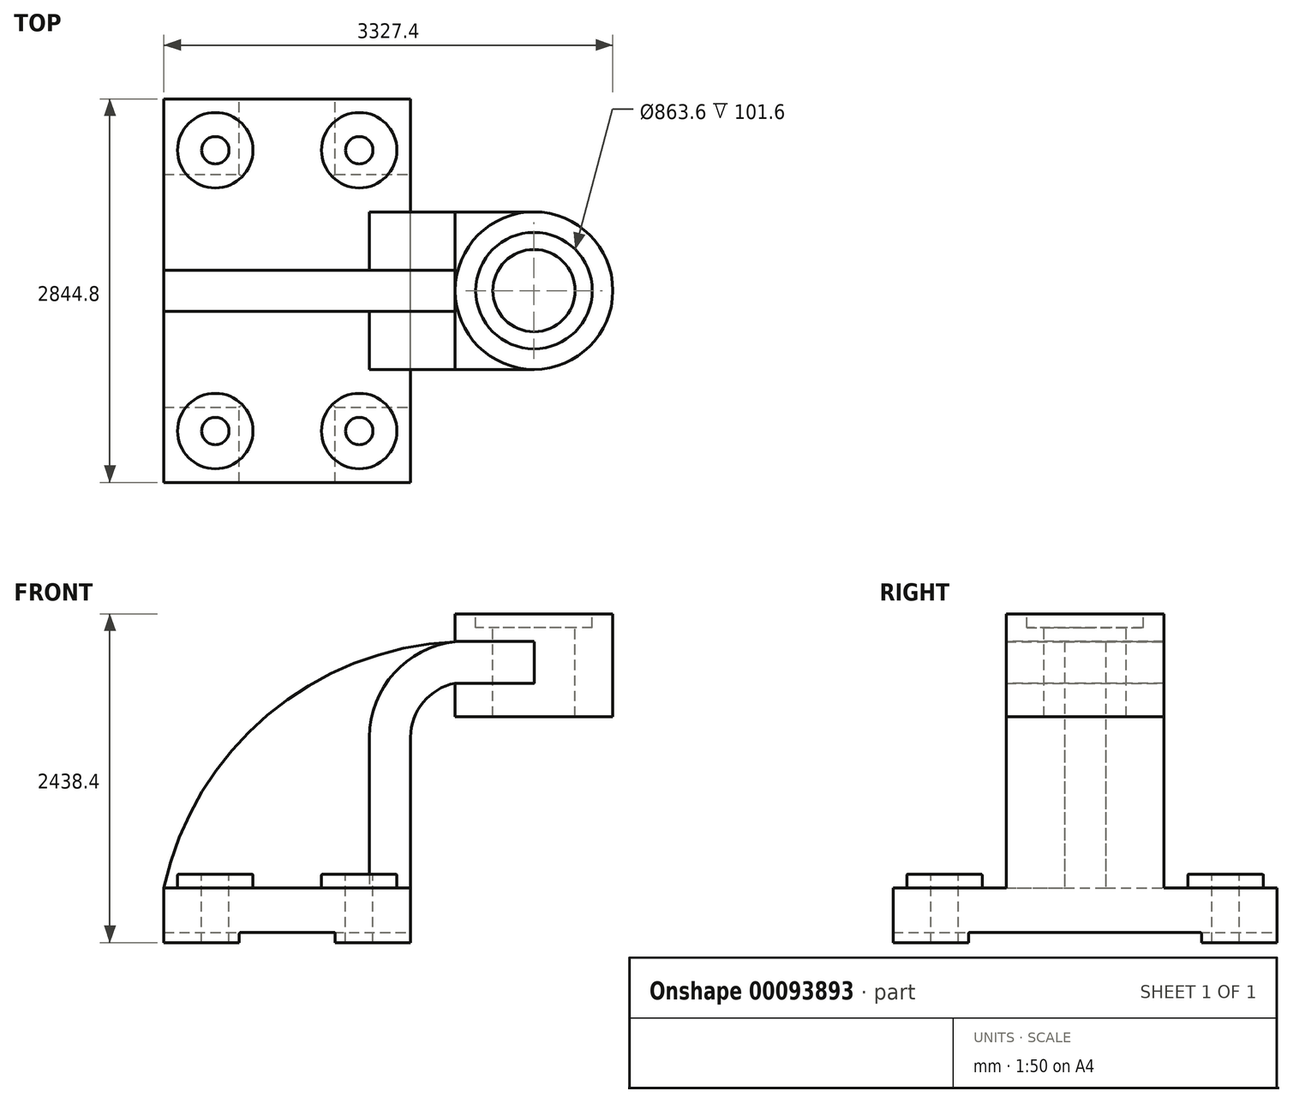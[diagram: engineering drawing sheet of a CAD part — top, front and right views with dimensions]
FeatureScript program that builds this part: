
annotation { "Feature Type Name" : "Feature", "Feature Type Description" : "" }
export const myFeature = defineFeature(function(context is Context, id is Id, definition is map)
    precondition{}
    {
        {
            var Q0;
            Q0=qCreatedBy(makeId("Front.planeOp"),FACE);
            var sketch = newSketch(context, id + "F0", { "sketchPlane" : qUnion([Q0])});
            skLineSegment(sketch, "E0", {"start": v(0, 0) * mm, "end": v(0, 1117.6) * mm});
            skLineSegment(sketch, "E1", {"start": v(406.4, 1524) * mm, "end": v(914.4, 1524) * mm});
            skLineSegment(sketch, "E2", {"start": v(-563.11, 0) * mm, "end": v(-1828.8, 0) * mm});
            skLineSegment(sketch, "E3", {"start": v(-1828.8, 0) * mm, "end": v(-1828.8, -406.4) * mm});
            skLineSegment(sketch, "E4", {"start": v(-1828.8, -406.4) * mm, "end": v(0, -406.4) * mm});
            skLineSegment(sketch, "E5", {"start": v(0, -406.4) * mm, "end": v(0, 0) * mm});
            skLineSegment(sketch, "E6", {"start": v(914.4, 1828.8) * mm, "end": v(914.4, 1524) * mm});
            skLineSegment(sketch, "E7", {"start": v(330.2, 2032) * mm, "end": v(330.2, 1270) * mm});
            skLineSegment(sketch, "E8", {"start": v(330.2, 1270) * mm, "end": v(1498.6, 1270) * mm});
            skLineSegment(sketch, "E9", {"start": v(1498.6, 1270) * mm, "end": v(1498.6, 2032) * mm});
            skLineSegment(sketch, "E10", {"start": v(1498.6, 2032) * mm, "end": v(330.2, 2032) * mm});
            skArc(sketch, "E11", {"start": v(330.2, 1824.7) * mm, "mid": v(-1060.76, 1280.87) * mm, "end": v(-1828.8, 0) * mm});
            skLineSegment(sketch, "E12", {"start": v(0, 0) * mm, "end": v(-1828.8, 0) * mm});
            skPoint(sketch, "E13.visualSharp", {"position": v(0, 1524) * mm});
            skArc(sketch, "E13.filletArc", {"start": v(406.4, 1524) * mm, "mid": v(119.03, 1404.97) * mm, "end": v(0, 1117.6) * mm});
            skLineSegment(sketch, "E14", {"start": v(-304.8, 1117.6) * mm, "end": v(-304.8, 0) * mm});
            skArc(sketch, "E15", {"start": v(-304.8, 1117.6) * mm, "mid": v(-122.75, 1592.8) * mm, "end": v(330.2, 1824.7) * mm});
            skPoint(sketch, "E16.endSnap0", {"position": v(-1828.8, -203.2) * mm});
            skLineSegment(sketch, "E17", {"start": v(-558.8, -406.4) * mm, "end": v(-558.8, -342.9) * mm});
            skLineSegment(sketch, "E18", {"start": v(-571.5, -330.2) * mm, "end": v(-1257.3, -330.2) * mm});
            skLineSegment(sketch, "E19", {"start": v(-1270, -342.9) * mm, "end": v(-1270, -406.4) * mm});
            skLineSegment(sketch, "E20", {"start": v(914.4, 2032) * mm, "end": v(914.4, 1270) * mm});
            skPoint(sketch, "E21", {"position": v(330.2, 1824.7) * mm});
            skPoint(sketch, "E22", {"position": v(330.2, 1516.8) * mm});
            skPoint(sketch, "E23.visualSharp", {"position": v(-558.8, -330.2) * mm});
            skArc(sketch, "E23.filletArc", {"start": v(-558.8, -342.9) * mm, "mid": v(-562.52, -333.92) * mm, "end": v(-571.5, -330.2) * mm});
            skPoint(sketch, "E24.visualSharp", {"position": v(-1270, -330.2) * mm});
            skArc(sketch, "E24.filletArc", {"start": v(-1257.3, -330.2) * mm, "mid": v(-1266.28, -333.92) * mm, "end": v(-1270, -342.9) * mm});
            skSolve(sketch);
        }
        {
            var Q0;
            Q0=qCreatedBy(makeId("Top.planeOp"),FACE);
            var sketch = newSketch(context, id + "F1", { "sketchPlane" : qUnion([Q0])});
            skLineSegment(sketch, "E25", {"start": v(-1828.8, 0) * mm, "end": v(-1828.8, 1422.4) * mm});
            skLineSegment(sketch, "E26", {"start": v(-1828.8, 1422.4) * mm, "end": v(0, 1422.4) * mm});
            skLineSegment(sketch, "E27", {"start": v(0, 1422.4) * mm, "end": v(0, -1422.4) * mm});
            skLineSegment(sketch, "E28", {"start": v(0, -1422.4) * mm, "end": v(-1828.8, -1422.4) * mm});
            skLineSegment(sketch, "E29", {"start": v(-1828.8, -1422.4) * mm, "end": v(-1828.8, 0) * mm});
            skCircle(sketch, "E30", {"center": v(-1447.8, -1041.4) * mm, "radius": 279.4 * mm});
            skCircle(sketch, "E31", {"center": v(-1447.8, 1041.4) * mm, "radius": 279.4 * mm});
            skCircle(sketch, "E32", {"center": v(-381, 1041.4) * mm, "radius": 279.4 * mm});
            skCircle(sketch, "E33", {"center": v(-381, -1041.4) * mm, "radius": 279.4 * mm});
            skCircle(sketch, "E34", {"center": v(-1447.8, 1041.4) * mm, "radius": 101.6 * mm});
            skCircle(sketch, "E35", {"center": v(-381, 1041.4) * mm, "radius": 101.6 * mm});
            skCircle(sketch, "E36", {"center": v(-1447.8, -1041.4) * mm, "radius": 101.6 * mm});
            skCircle(sketch, "E37", {"center": v(-381, -1041.4) * mm, "radius": 101.6 * mm});
            skSolve(sketch);
        }
        {
            var Q0;
            {var subQ1=sQuery(id+"F0.wireOp",EDGE,"E9");Q0=makeQuery(id+"F0.imprint","IMPRINT",FACE,{"disambiguationData":[TD([[makeQuery(id+"F0.imprint","IMPRINT",EDGE,{"derivedFrom":subQ1}),1.0]])]});}
            var Q1;
            Q1=sQuery(id+"F0.wireOp",EDGE,"E20");
            revolve(context, id + "F2", {"entities" : qUnion([Q0]), "axis" : qUnion([Q1]), "revolveType" : RevolveType.FULL});
        }
        {
            var Q0;
            {var subQ8=sQuery(id+"F0.wireOp",EDGE,"E0");Q0=makeQuery(id+"F0.imprint","IMPRINT",FACE,{"disambiguationData":[TD([[makeQuery(id+"F0.imprint","IMPRINT",EDGE,{"derivedFrom":subQ8}),1.0]])]});}
            extrude(context, id + "F3", {"entities" : qUnion([Q0]), "endBound" : BoundingType.SYMMETRIC, "depth" : 1168.4 * mm});
        }
        {
            var Q0;
            Q0=makeQuery(id+"F3.opExtrude","SWEPT_FACE",FACE,{"disambiguationData":[OSD([sQuery(id+"F0.wireOp",EDGE,"E7")])]});
            extrude(context, id + "F4", {"entities" : qUnion([Q0]), "depth" : 584.57 * mm});
        }
        {
            var Q0;
            Q0=makeQuery(id+"F2.opRevolve","SWEPT_BODY",BODY,{"disambiguationData":[OSD([sQuery(id+"F0.wireOp",EDGE,"E8"),sQuery(id+"F0.wireOp",EDGE,"E9"),sQuery(id+"F0.wireOp",EDGE,"E10"),sQuery(id+"F0.wireOp",EDGE,"E20")])]});
            var Q1;
            Q1=makeQuery(id+"F3.opExtrude","SWEPT_BODY",BODY,{"disambiguationData":[OSD([sQuery(id+"F0.wireOp",EDGE,"E0"),sQuery(id+"F0.wireOp",EDGE,"E1"),sQuery(id+"F0.wireOp",EDGE,"Te8mhpom-QYgg-O1N1-Xy0P-BGKtfm83w9Aw"),sQuery(id+"F0.wireOp",EDGE,"E7"),sQuery(id+"F0.wireOp",EDGE,"E11"),sQuery(id+"F0.wireOp",EDGE,"E12"),sQuery(id+"F0.wireOp",EDGE,"E13.filletArc"),sQuery(id+"F0.wireOp",EDGE,"E14"),sQuery(id+"F0.wireOp",EDGE,"E15")])]});
            var Q2;
            Q2=makeQuery(id+"F4.opExtrude","SWEPT_BODY",BODY,{"disambiguationData":[OSD([sQuery(id+"F0.wireOp",EDGE,"E7")])]});
            booleanBodies(context, id + "F5", {"operationType" : BooleanOperationType.UNION, "tools" : qUnion([Q0, Q1, Q2])});
        }
        {
            var Q0;
            {var subQ0=sQuery(id+"F0.wireOp",EDGE,"E14");Q0=makeQuery(id+"F0.imprint","IMPRINT",FACE,{"disambiguationData":[TD([[makeQuery(id+"F0.imprint","IMPRINT",EDGE,{"derivedFrom":subQ0}),-1.0]])]});}
            extrude(context, id + "F6", {"entities" : qUnion([Q0]), "endBound" : BoundingType.SYMMETRIC, "depth" : 304.8 * mm});
        }
        {
            var Q0;
            Q0=makeQuery(id+"F1.imprint","IMPRINT",FACE,{"disambiguationData":[TD([[makeQuery(id+"F1.imprint","IMPRINT",EDGE,{"derivedFrom":sQuery(id+"F1.wireOp",EDGE,"E25")}),-1.0]])]});
            var Q1;
            Q1=makeQuery(id+"F1.imprint","IMPRINT",FACE,{"disambiguationData":[TD([[makeQuery(id+"F1.imprint","IMPRINT",EDGE,{"derivedFrom":sQuery(id+"F1.wireOp",EDGE,"E30")}),1.0]])]});
            var Q2;
            Q2=makeQuery(id+"F1.imprint","IMPRINT",FACE,{"disambiguationData":[TD([[makeQuery(id+"F1.imprint","IMPRINT",EDGE,{"derivedFrom":sQuery(id+"F1.wireOp",EDGE,"E33")}),1.0]])]});
            var Q3;
            Q3=makeQuery(id+"F1.imprint","IMPRINT",FACE,{"disambiguationData":[TD([[makeQuery(id+"F1.imprint","IMPRINT",EDGE,{"derivedFrom":sQuery(id+"F1.wireOp",EDGE,"E32")}),1.0]])]});
            var Q4;
            Q4=makeQuery(id+"F1.imprint","IMPRINT",FACE,{"disambiguationData":[TD([[makeQuery(id+"F1.imprint","IMPRINT",EDGE,{"derivedFrom":sQuery(id+"F1.wireOp",EDGE,"E31")}),1.0]])]});
            extrude(context, id + "F7", {"entities" : qUnion([Q0, Q1, Q2, Q3, Q4]), "operationType" : NewBodyOperationType.ADD, "oppositeDirection" : true, "depth" : 406.4 * mm});
        }
        {
            var Q0;
            Q0=makeQuery(id+"F1.imprint","IMPRINT",FACE,{"disambiguationData":[TD([[makeQuery(id+"F1.imprint","IMPRINT",EDGE,{"derivedFrom":sQuery(id+"F1.wireOp",EDGE,"E30")}),1.0]])]});
            var Q1;
            Q1=makeQuery(id+"F1.imprint","IMPRINT",FACE,{"disambiguationData":[TD([[makeQuery(id+"F1.imprint","IMPRINT",EDGE,{"derivedFrom":sQuery(id+"F1.wireOp",EDGE,"E33")}),1.0]])]});
            var Q2;
            Q2=makeQuery(id+"F1.imprint","IMPRINT",FACE,{"disambiguationData":[TD([[makeQuery(id+"F1.imprint","IMPRINT",EDGE,{"derivedFrom":sQuery(id+"F1.wireOp",EDGE,"E32")}),1.0]])]});
            var Q3;
            Q3=makeQuery(id+"F1.imprint","IMPRINT",FACE,{"disambiguationData":[TD([[makeQuery(id+"F1.imprint","IMPRINT",EDGE,{"derivedFrom":sQuery(id+"F1.wireOp",EDGE,"E31")}),1.0]])]});
            extrude(context, id + "F8", {"entities" : qUnion([Q0, Q1, Q2, Q3]), "operationType" : NewBodyOperationType.ADD, "depth" : 101.6 * mm});
        }
        {
            var Q0;
            {var subQ0=sQuery(id+"F0.wireOp",EDGE,"E17");Q0=makeQuery(id+"F0.imprint","IMPRINT",FACE,{"disambiguationData":[TD([[makeQuery(id+"F0.imprint","IMPRINT",EDGE,{"derivedFrom":subQ0}),1.0]])]});}
            extrude(context, id + "F9", {"entities" : qUnion([Q0]), "operationType" : NewBodyOperationType.REMOVE, "endBound" : BoundingType.THROUGH_ALL, "depth" : 25.4 * mm});
        }
        {
            var Q0;
            {var subQ0=sQuery(id+"F0.wireOp",EDGE,"E17");Q0=makeQuery(id+"F0.imprint","IMPRINT",FACE,{"disambiguationData":[TD([[makeQuery(id+"F0.imprint","IMPRINT",EDGE,{"derivedFrom":subQ0}),1.0]])]});}
            extrude(context, id + "F10", {"entities" : qUnion([Q0]), "operationType" : NewBodyOperationType.REMOVE, "endBound" : BoundingType.THROUGH_ALL, "oppositeDirection" : true, "depth" : 25.4 * mm});
        }
        {
            var Q0;
            {var subQ0=sQuery(id+"F0.wireOp",EDGE,"E15");var subQ1=sQuery(id+"F0.wireOp",EDGE,"E7");var subQ2=makeQuery(id+"F4.opExtrude","SWEPT_FACE",FACE,{"disambiguationData":[OSD([subQ1,subQ0])]});Q0=makeQuery(id+"F5.opBoolean","SPLIT",FACE,{"disambiguationData":[TD([makeQuery(id+"F2.opRevolve","SWEPT_FACE",FACE,{"disambiguationData":[OSD([sQuery(id+"F0.wireOp",EDGE,"E9")])]}),makeQuery(id+"F3.opExtrude","CAP_FACE",FACE,{"disambiguationData":[OSD([sQuery(id+"F0.wireOp",EDGE,"E0"),subQ1,sQuery(id+"F0.wireOp",EDGE,"E12"),sQuery(id+"F0.wireOp",EDGE,"E13.filletArc"),sQuery(id+"F0.wireOp",EDGE,"E14"),subQ0])],"isStart":false}),makeQuery(id+"F3.opExtrude","SWEPT_FACE",FACE,{"disambiguationData":[OSD([subQ0])]}),subQ2,makeQuery(id+"F4.opExtrude","SWEPT_FACE",FACE,{"disambiguationData":[OSD([subQ1]),TDD([makeQuery(id+"F3.opExtrude","CAP_EDGE",EDGE,{"disambiguationData":[OSD([subQ1])],"isStart":false})])]})])],"derivedFrom":subQ2});}
            var Q1;
            {var subQ0=sQuery(id+"F0.wireOp",EDGE,"E15");var subQ1=sQuery(id+"F0.wireOp",EDGE,"E7");var subQ2=makeQuery(id+"F4.opExtrude","SWEPT_FACE",FACE,{"disambiguationData":[OSD([subQ1,subQ0])]});Q1=makeQuery(id+"F5.opBoolean","SPLIT",FACE,{"disambiguationData":[TD([makeQuery(id+"F2.opRevolve","SWEPT_FACE",FACE,{"disambiguationData":[OSD([sQuery(id+"F0.wireOp",EDGE,"E9")])]}),makeQuery(id+"F3.opExtrude","CAP_FACE",FACE,{"disambiguationData":[OSD([sQuery(id+"F0.wireOp",EDGE,"E0"),subQ1,sQuery(id+"F0.wireOp",EDGE,"E12"),sQuery(id+"F0.wireOp",EDGE,"E13.filletArc"),sQuery(id+"F0.wireOp",EDGE,"E14"),subQ0])],"isStart":true}),makeQuery(id+"F3.opExtrude","SWEPT_FACE",FACE,{"disambiguationData":[OSD([subQ0])]}),subQ2,makeQuery(id+"F4.opExtrude","SWEPT_FACE",FACE,{"disambiguationData":[OSD([subQ1]),TDD([makeQuery(id+"F3.opExtrude","CAP_EDGE",EDGE,{"disambiguationData":[OSD([subQ1])],"isStart":true})])]})])],"derivedFrom":subQ2});}
            extrude(context, id + "F11", {"entities" : qUnion([Q0, Q1]), "operationType" : NewBodyOperationType.ADD, "depth" : 2.3 * mm});
        }
        {
            var Q0;
            Q0=makeQuery(id+"F2.opRevolve","SWEPT_FACE",FACE,{"disambiguationData":[OSD([sQuery(id+"F0.wireOp",EDGE,"E10")])]});
            var sketch = newSketch(context, id + "F12", { "sketchPlane" : qUnion([Q0])});
            skPoint(sketch, "E38.0", {"position": v(914.4, 0) * mm});
            skCircle(sketch, "E39", {"center": v(914.4, 0) * mm, "radius": 304.8 * mm});
            skCircle(sketch, "E40", {"center": v(914.4, 0) * mm, "radius": 431.8 * mm});
            skSolve(sketch);
        }
        {
            var Q0;
            Q0=makeQuery(id+"F12.imprint","IMPRINT",FACE,{"disambiguationData":[TD([[makeQuery(id+"F12.imprint","IMPRINT",EDGE,{"derivedFrom":sQuery(id+"F12.wireOp",EDGE,"E39")}),1.0]])]});
            extrude(context, id + "F13", {"entities" : qUnion([Q0]), "operationType" : NewBodyOperationType.REMOVE, "endBound" : BoundingType.THROUGH_ALL, "oppositeDirection" : true, "depth" : 25.4 * mm});
        }
        {
            var Q0;
            Q0=makeQuery(id+"F12.imprint","IMPRINT",FACE,{"disambiguationData":[TD([[makeQuery(id+"F12.imprint","IMPRINT",EDGE,{"derivedFrom":sQuery(id+"F12.wireOp",EDGE,"E39")}),-1.0]])]});
            extrude(context, id + "F14", {"entities" : qUnion([Q0]), "operationType" : NewBodyOperationType.REMOVE, "oppositeDirection" : true, "depth" : 101.6 * mm});
        }
        {
            var Q0;
            Q0=makeQuery(id+"F7.boolean.opBoolean","MERGE",FACE,{"derivedFrom":[makeQuery(id+"F3.opExtrude","SWEPT_FACE",FACE,{"disambiguationData":[OSD([sQuery(id+"F0.wireOp",EDGE,"E0")])]}),makeQuery(id+"F7.opExtrude","SWEPT_FACE",FACE,{"disambiguationData":[OSD([sQuery(id+"F1.wireOp",EDGE,"E27")])]})]});
            var sketch = newSketch(context, id + "F15", { "sketchPlane" : qUnion([Q0])});
            skLineSegment(sketch, "E41", {"start": v(-863.6, -406.4) * mm, "end": v(-863.6, -342.9) * mm});
            skLineSegment(sketch, "E42", {"start": v(-850.9, -330.2) * mm, "end": v(850.9, -330.2) * mm});
            skLineSegment(sketch, "E43", {"start": v(863.6, -342.9) * mm, "end": v(863.6, -406.4) * mm});
            skPoint(sketch, "E44.visualSharp", {"position": v(-863.6, -330.2) * mm});
            skArc(sketch, "E44.filletArc", {"start": v(-850.9, -330.2) * mm, "mid": v(-859.88, -333.92) * mm, "end": v(-863.6, -342.9) * mm});
            skPoint(sketch, "E45.visualSharp", {"position": v(863.6, -330.2) * mm});
            skArc(sketch, "E45.filletArc", {"start": v(863.6, -342.9) * mm, "mid": v(859.88, -333.92) * mm, "end": v(850.9, -330.2) * mm});
            skSolve(sketch);
        }
        {
            var Q0;
            {var subQ0=sQuery(id+"F15.wireOp",EDGE,"E41");Q0=makeQuery(id+"F15.imprint","IMPRINT",FACE,{"disambiguationData":[TD([[makeQuery(id+"F15.imprint","IMPRINT",EDGE,{"derivedFrom":subQ0}),-1.0]])]});}
            extrude(context, id + "F16", {"entities" : qUnion([Q0]), "operationType" : NewBodyOperationType.REMOVE, "endBound" : BoundingType.THROUGH_ALL, "oppositeDirection" : true, "depth" : 25.4 * mm});
        }
        {
            var Q0;
            Q0=makeQuery(id+"F8.opExtrude","SWEPT_FACE",FACE,{"disambiguationData":[OSD([sQuery(id+"F1.wireOp",EDGE,"E30")])]});
            var Q1;
            Q1=makeQuery(id+"F8.opExtrude","SWEPT_FACE",FACE,{"disambiguationData":[OSD([sQuery(id+"F1.wireOp",EDGE,"E33")])]});
            var Q2;
            Q2=makeQuery(id+"F8.opExtrude","SWEPT_FACE",FACE,{"disambiguationData":[OSD([sQuery(id+"F1.wireOp",EDGE,"E32")])]});
            fillet(context, id + "F17", {"entities" : qUnion([Q0, Q1, Q2]), "radius" : 10.16 * mm, "tangentPropagation" : true, "allowEdgeOverflow" : false});
        }
    });
